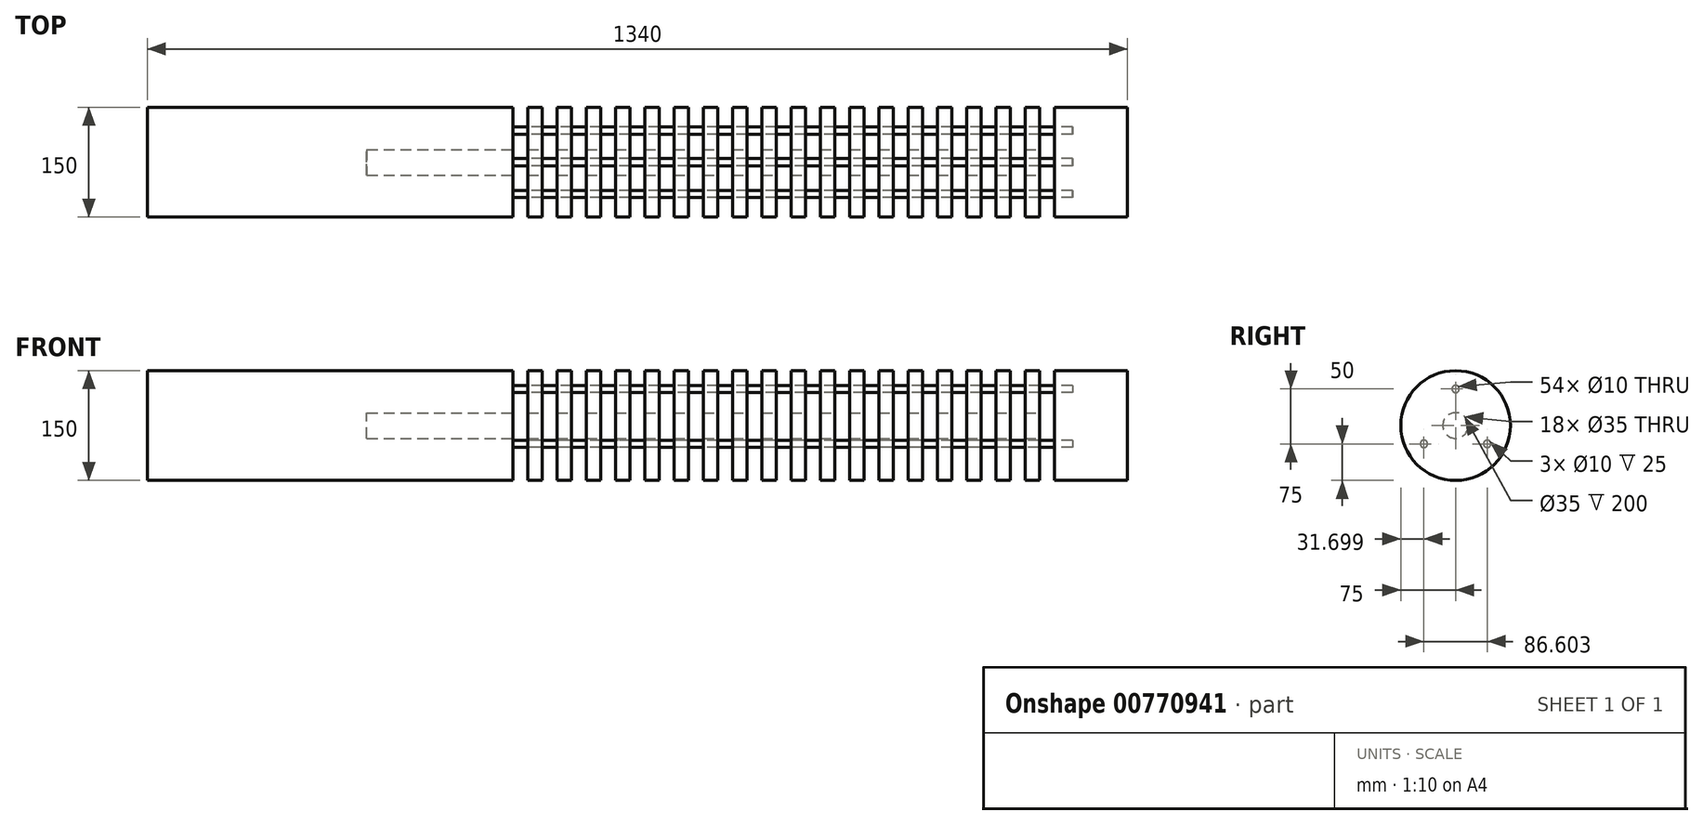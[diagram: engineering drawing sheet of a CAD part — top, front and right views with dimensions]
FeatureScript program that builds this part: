
annotation { "Feature Type Name" : "Feature", "Feature Type Description" : "" }
export const myFeature = defineFeature(function(context is Context, id is Id, definition is map)
    precondition{}
    {
        {
            var Q0;
            Q0=qCreatedBy(makeId("Top.planeOp"),FACE);
            var sketch = newSketch(context, id + "F0", { "sketchPlane" : qUnion([Q0])});
            skLineSegment(sketch, "E0", {"start": v(-500, 0) * mm, "end": v(-500, -75) * mm});
            skLineSegment(sketch, "E1", {"start": v(-500, -75) * mm, "end": v(0, -75) * mm});
            skLineSegment(sketch, "E2", {"start": v(0, -75) * mm, "end": v(0, -17.5) * mm});
            skLineSegment(sketch, "E3", {"start": v(0, -17.5) * mm, "end": v(-200, -17.5) * mm});
            skLineSegment(sketch, "E4", {"start": v(-200, -17.5) * mm, "end": v(-200, 0) * mm});
            skLineSegment(sketch, "E5", {"start": v(-200, 0) * mm, "end": v(-500, 0) * mm});
            skSolve(sketch);
        }
        {
            var Q0;
            Q0=qCreatedBy(makeId("Top.planeOp"),FACE);
            var sketch = newSketch(context, id + "F1", { "sketchPlane" : qUnion([Q0])});
            skLineSegment(sketch, "E6.bottom", {"start": v(20, -17.5) * mm, "end": v(40, -17.5) * mm});
            skLineSegment(sketch, "E6.top", {"start": v(20, -75) * mm, "end": v(40, -75) * mm});
            skLineSegment(sketch, "E6.left", {"start": v(20, -17.5) * mm, "end": v(20, -75) * mm});
            skLineSegment(sketch, "E6.right", {"start": v(40, -17.5) * mm, "end": v(40, -75) * mm});
            skLineSegment(sketch, "E7.1.0.0", {"start": v(60, -75) * mm, "end": v(80, -75) * mm});
            skLineSegment(sketch, "E7.1.0.1", {"start": v(80, -17.5) * mm, "end": v(80, -75) * mm});
            skLineSegment(sketch, "E7.1.0.2", {"start": v(60, -17.5) * mm, "end": v(60, -75) * mm});
            skLineSegment(sketch, "E7.1.0.3", {"start": v(60, -17.5) * mm, "end": v(80, -17.5) * mm});
            skLineSegment(sketch, "E7.2.0.0", {"start": v(100, -75) * mm, "end": v(120, -75) * mm});
            skLineSegment(sketch, "E7.2.0.1", {"start": v(120, -17.5) * mm, "end": v(120, -75) * mm});
            skLineSegment(sketch, "E7.2.0.2", {"start": v(100, -17.5) * mm, "end": v(100, -75) * mm});
            skLineSegment(sketch, "E7.2.0.3", {"start": v(100, -17.5) * mm, "end": v(120, -17.5) * mm});
            skLineSegment(sketch, "E7.3.0.0", {"start": v(140, -75) * mm, "end": v(160, -75) * mm});
            skLineSegment(sketch, "E7.3.0.1", {"start": v(160, -17.5) * mm, "end": v(160, -75) * mm});
            skLineSegment(sketch, "E7.3.0.2", {"start": v(140, -17.5) * mm, "end": v(140, -75) * mm});
            skLineSegment(sketch, "E7.3.0.3", {"start": v(140, -17.5) * mm, "end": v(160, -17.5) * mm});
            skLineSegment(sketch, "E7.4.0.0", {"start": v(180, -75) * mm, "end": v(200, -75) * mm});
            skLineSegment(sketch, "E7.4.0.1", {"start": v(200, -17.5) * mm, "end": v(200, -75) * mm});
            skLineSegment(sketch, "E7.4.0.2", {"start": v(180, -17.5) * mm, "end": v(180, -75) * mm});
            skLineSegment(sketch, "E7.4.0.3", {"start": v(180, -17.5) * mm, "end": v(200, -17.5) * mm});
            skLineSegment(sketch, "E7.5.0.0", {"start": v(220, -75) * mm, "end": v(240, -75) * mm});
            skLineSegment(sketch, "E7.5.0.1", {"start": v(240, -17.5) * mm, "end": v(240, -75) * mm});
            skLineSegment(sketch, "E7.5.0.2", {"start": v(220, -17.5) * mm, "end": v(220, -75) * mm});
            skLineSegment(sketch, "E7.5.0.3", {"start": v(220, -17.5) * mm, "end": v(240, -17.5) * mm});
            skLineSegment(sketch, "E7.6.0.0", {"start": v(260, -75) * mm, "end": v(280, -75) * mm});
            skLineSegment(sketch, "E7.6.0.1", {"start": v(280, -17.5) * mm, "end": v(280, -75) * mm});
            skLineSegment(sketch, "E7.6.0.2", {"start": v(260, -17.5) * mm, "end": v(260, -75) * mm});
            skLineSegment(sketch, "E7.6.0.3", {"start": v(260, -17.5) * mm, "end": v(280, -17.5) * mm});
            skLineSegment(sketch, "E7.7.0.0", {"start": v(300, -75) * mm, "end": v(320, -75) * mm});
            skLineSegment(sketch, "E7.7.0.1", {"start": v(320, -17.5) * mm, "end": v(320, -75) * mm});
            skLineSegment(sketch, "E7.7.0.2", {"start": v(300, -17.5) * mm, "end": v(300, -75) * mm});
            skLineSegment(sketch, "E7.7.0.3", {"start": v(300, -17.5) * mm, "end": v(320, -17.5) * mm});
            skLineSegment(sketch, "E7.8.0.0", {"start": v(340, -75) * mm, "end": v(360, -75) * mm});
            skLineSegment(sketch, "E7.8.0.1", {"start": v(360, -17.5) * mm, "end": v(360, -75) * mm});
            skLineSegment(sketch, "E7.8.0.2", {"start": v(340, -17.5) * mm, "end": v(340, -75) * mm});
            skLineSegment(sketch, "E7.8.0.3", {"start": v(340, -17.5) * mm, "end": v(360, -17.5) * mm});
            skLineSegment(sketch, "E7.9.0.0", {"start": v(380, -75) * mm, "end": v(400, -75) * mm});
            skLineSegment(sketch, "E7.9.0.1", {"start": v(400, -17.5) * mm, "end": v(400, -75) * mm});
            skLineSegment(sketch, "E7.9.0.2", {"start": v(380, -17.5) * mm, "end": v(380, -75) * mm});
            skLineSegment(sketch, "E7.9.0.3", {"start": v(380, -17.5) * mm, "end": v(400, -17.5) * mm});
            skLineSegment(sketch, "E7.10.0.0", {"start": v(420, -75) * mm, "end": v(440, -75) * mm});
            skLineSegment(sketch, "E7.10.0.1", {"start": v(440, -17.5) * mm, "end": v(440, -75) * mm});
            skLineSegment(sketch, "E7.10.0.2", {"start": v(420, -17.5) * mm, "end": v(420, -75) * mm});
            skLineSegment(sketch, "E7.10.0.3", {"start": v(420, -17.5) * mm, "end": v(440, -17.5) * mm});
            skLineSegment(sketch, "E7.11.0.0", {"start": v(460, -75) * mm, "end": v(480, -75) * mm});
            skLineSegment(sketch, "E7.11.0.1", {"start": v(480, -17.5) * mm, "end": v(480, -75) * mm});
            skLineSegment(sketch, "E7.11.0.2", {"start": v(460, -17.5) * mm, "end": v(460, -75) * mm});
            skLineSegment(sketch, "E7.11.0.3", {"start": v(460, -17.5) * mm, "end": v(480, -17.5) * mm});
            skLineSegment(sketch, "E7.12.0.0", {"start": v(500, -75) * mm, "end": v(520, -75) * mm});
            skLineSegment(sketch, "E7.12.0.1", {"start": v(520, -17.5) * mm, "end": v(520, -75) * mm});
            skLineSegment(sketch, "E7.12.0.2", {"start": v(500, -17.5) * mm, "end": v(500, -75) * mm});
            skLineSegment(sketch, "E7.12.0.3", {"start": v(500, -17.5) * mm, "end": v(520, -17.5) * mm});
            skLineSegment(sketch, "E7.13.0.0", {"start": v(540, -75) * mm, "end": v(560, -75) * mm});
            skLineSegment(sketch, "E7.13.0.1", {"start": v(560, -17.5) * mm, "end": v(560, -75) * mm});
            skLineSegment(sketch, "E7.13.0.2", {"start": v(540, -17.5) * mm, "end": v(540, -75) * mm});
            skLineSegment(sketch, "E7.13.0.3", {"start": v(540, -17.5) * mm, "end": v(560, -17.5) * mm});
            skLineSegment(sketch, "E7.14.0.0", {"start": v(580, -75) * mm, "end": v(600, -75) * mm});
            skLineSegment(sketch, "E7.14.0.1", {"start": v(600, -17.5) * mm, "end": v(600, -75) * mm});
            skLineSegment(sketch, "E7.14.0.2", {"start": v(580, -17.5) * mm, "end": v(580, -75) * mm});
            skLineSegment(sketch, "E7.14.0.3", {"start": v(580, -17.5) * mm, "end": v(600, -17.5) * mm});
            skLineSegment(sketch, "E7.15.0.0", {"start": v(620, -75) * mm, "end": v(640, -75) * mm});
            skLineSegment(sketch, "E7.15.0.1", {"start": v(640, -17.5) * mm, "end": v(640, -75) * mm});
            skLineSegment(sketch, "E7.15.0.2", {"start": v(620, -17.5) * mm, "end": v(620, -75) * mm});
            skLineSegment(sketch, "E7.15.0.3", {"start": v(620, -17.5) * mm, "end": v(640, -17.5) * mm});
            skLineSegment(sketch, "E7.16.0.0", {"start": v(660, -75) * mm, "end": v(680, -75) * mm});
            skLineSegment(sketch, "E7.16.0.1", {"start": v(680, -17.5) * mm, "end": v(680, -75) * mm});
            skLineSegment(sketch, "E7.16.0.2", {"start": v(660, -17.5) * mm, "end": v(660, -75) * mm});
            skLineSegment(sketch, "E7.16.0.3", {"start": v(660, -17.5) * mm, "end": v(680, -17.5) * mm});
            skLineSegment(sketch, "E7.17.0.0", {"start": v(700, -75) * mm, "end": v(720, -75) * mm});
            skLineSegment(sketch, "E7.17.0.1", {"start": v(720, -17.5) * mm, "end": v(720, -75) * mm});
            skLineSegment(sketch, "E7.17.0.2", {"start": v(700, -17.5) * mm, "end": v(700, -75) * mm});
            skLineSegment(sketch, "E7.17.0.3", {"start": v(700, -17.5) * mm, "end": v(720, -17.5) * mm});
            skLineSegment(sketch, "E7.direction1", {"start": v(20, -75) * mm, "end": v(60, -75) * mm, "construction": true});
            skSolve(sketch);
        }
        {
            var Q0;
            Q0=qCreatedBy(makeId("Top.planeOp"),FACE);
            var sketch = newSketch(context, id + "F2", { "sketchPlane" : qUnion([Q0])});
            skLineSegment(sketch, "E8.bottom", {"start": v(740, -75) * mm, "end": v(840, -75) * mm});
            skLineSegment(sketch, "E8.top", {"start": v(740, 0) * mm, "end": v(840, 0) * mm});
            skLineSegment(sketch, "E8.left", {"start": v(740, -75) * mm, "end": v(740, 0) * mm});
            skLineSegment(sketch, "E8.right", {"start": v(840, -75) * mm, "end": v(840, 0) * mm});
            skSolve(sketch);
        }
        {
            var Q0;
            Q0=makeQuery(id+"F0.imprint","IMPRINT",FACE,{"disambiguationData":[TD([[makeQuery(id+"F0.imprint","IMPRINT",EDGE,{"derivedFrom":sQuery(id+"F0.wireOp",EDGE,"E0")}),1.0]])]});
            var Q1;
            Q1=makeQuery(id+"F1.imprint","IMPRINT",FACE,{"disambiguationData":[TD([[makeQuery(id+"F1.imprint","IMPRINT",EDGE,{"derivedFrom":sQuery(id+"F1.wireOp",EDGE,"E7.4.0.0")}),1.0]])]});
            var Q2;
            Q2=makeQuery(id+"F1.imprint","IMPRINT",FACE,{"disambiguationData":[TD([[makeQuery(id+"F1.imprint","IMPRINT",EDGE,{"derivedFrom":sQuery(id+"F1.wireOp",EDGE,"E7.9.0.0")}),1.0]])]});
            var Q3;
            Q3=makeQuery(id+"F1.imprint","IMPRINT",FACE,{"disambiguationData":[TD([[makeQuery(id+"F1.imprint","IMPRINT",EDGE,{"derivedFrom":sQuery(id+"F1.wireOp",EDGE,"E7.3.0.0")}),1.0]])]});
            var Q4;
            Q4=makeQuery(id+"F1.imprint","IMPRINT",FACE,{"disambiguationData":[TD([[makeQuery(id+"F1.imprint","IMPRINT",EDGE,{"derivedFrom":sQuery(id+"F1.wireOp",EDGE,"E7.2.0.0")}),1.0]])]});
            var Q5;
            Q5=makeQuery(id+"F1.imprint","IMPRINT",FACE,{"disambiguationData":[TD([[makeQuery(id+"F1.imprint","IMPRINT",EDGE,{"derivedFrom":sQuery(id+"F1.wireOp",EDGE,"E7.10.0.0")}),1.0]])]});
            var Q6;
            Q6=makeQuery(id+"F1.imprint","IMPRINT",FACE,{"disambiguationData":[TD([[makeQuery(id+"F1.imprint","IMPRINT",EDGE,{"derivedFrom":sQuery(id+"F1.wireOp",EDGE,"E7.1.0.0")}),1.0]])]});
            var Q7;
            Q7=makeQuery(id+"F1.imprint","IMPRINT",FACE,{"disambiguationData":[TD([[makeQuery(id+"F1.imprint","IMPRINT",EDGE,{"derivedFrom":sQuery(id+"F1.wireOp",EDGE,"E7.8.0.0")}),1.0]])]});
            var Q8;
            Q8=makeQuery(id+"F1.imprint","IMPRINT",FACE,{"disambiguationData":[TD([[makeQuery(id+"F1.imprint","IMPRINT",EDGE,{"derivedFrom":sQuery(id+"F1.wireOp",EDGE,"E7.17.0.0")}),1.0]])]});
            var Q9;
            Q9=makeQuery(id+"F1.imprint","IMPRINT",FACE,{"disambiguationData":[TD([[makeQuery(id+"F1.imprint","IMPRINT",EDGE,{"derivedFrom":sQuery(id+"F1.wireOp",EDGE,"E7.16.0.0")}),1.0]])]});
            var Q10;
            Q10=makeQuery(id+"F1.imprint","IMPRINT",FACE,{"disambiguationData":[TD([[makeQuery(id+"F1.imprint","IMPRINT",EDGE,{"derivedFrom":sQuery(id+"F1.wireOp",EDGE,"E7.12.0.0")}),1.0]])]});
            var Q11;
            Q11=makeQuery(id+"F1.imprint","IMPRINT",FACE,{"disambiguationData":[TD([[makeQuery(id+"F1.imprint","IMPRINT",EDGE,{"derivedFrom":sQuery(id+"F1.wireOp",EDGE,"E7.5.0.0")}),1.0]])]});
            var Q12;
            Q12=makeQuery(id+"F1.imprint","IMPRINT",FACE,{"disambiguationData":[TD([[makeQuery(id+"F1.imprint","IMPRINT",EDGE,{"derivedFrom":sQuery(id+"F1.wireOp",EDGE,"E7.6.0.0")}),1.0]])]});
            var Q13;
            Q13=makeQuery(id+"F1.imprint","IMPRINT",FACE,{"disambiguationData":[TD([[makeQuery(id+"F1.imprint","IMPRINT",EDGE,{"derivedFrom":sQuery(id+"F1.wireOp",EDGE,"E7.11.0.0")}),1.0]])]});
            var Q14;
            Q14=makeQuery(id+"F1.imprint","IMPRINT",FACE,{"disambiguationData":[TD([[makeQuery(id+"F1.imprint","IMPRINT",EDGE,{"derivedFrom":sQuery(id+"F1.wireOp",EDGE,"E7.7.0.0")}),1.0]])]});
            var Q15;
            Q15=makeQuery(id+"F1.imprint","IMPRINT",FACE,{"disambiguationData":[TD([[makeQuery(id+"F1.imprint","IMPRINT",EDGE,{"derivedFrom":sQuery(id+"F1.wireOp",EDGE,"E6.bottom")}),-1.0]])]});
            var Q16;
            Q16=makeQuery(id+"F1.imprint","IMPRINT",FACE,{"disambiguationData":[TD([[makeQuery(id+"F1.imprint","IMPRINT",EDGE,{"derivedFrom":sQuery(id+"F1.wireOp",EDGE,"E7.14.0.0")}),1.0]])]});
            var Q17;
            Q17=makeQuery(id+"F1.imprint","IMPRINT",FACE,{"disambiguationData":[TD([[makeQuery(id+"F1.imprint","IMPRINT",EDGE,{"derivedFrom":sQuery(id+"F1.wireOp",EDGE,"E7.13.0.0")}),1.0]])]});
            var Q18;
            Q18=makeQuery(id+"F2.imprint","IMPRINT",FACE,{"disambiguationData":[TD([[makeQuery(id+"F2.imprint","IMPRINT",EDGE,{"derivedFrom":sQuery(id+"F2.wireOp",EDGE,"E8.bottom")}),1.0]])]});
            var Q19;
            Q19=makeQuery(id+"F1.imprint","IMPRINT",FACE,{"disambiguationData":[TD([[makeQuery(id+"F1.imprint","IMPRINT",EDGE,{"derivedFrom":sQuery(id+"F1.wireOp",EDGE,"E7.15.0.0")}),1.0]])]});
            var Q20;
            Q20=sQuery(id+"F0.wireOp",EDGE,"E5");
            revolve(context, id + "F3", {"surfaceOperationType" : NewSurfaceOperationType.NEW, "entities" : qUnion([Q0, Q1, Q2, Q3, Q4, Q5, Q6, Q7, Q8, Q9, Q10, Q11, Q12, Q13, Q14, Q15, Q16, Q17, Q18, Q19]), "axis" : qUnion([Q20]), "revolveType" : RevolveType.FULL});
        }
        {
            var Q0;
            Q0=qCreatedBy(makeId("Right.planeOp"),FACE);
            var sketch = newSketch(context, id + "F4", { "sketchPlane" : qUnion([Q0])});
            skCircle(sketch, "E9", {"center": v(0, 50) * mm, "radius": 5 * mm});
            skCircle(sketch, "E10.1.0", {"center": v(-43.3, -25) * mm, "radius": 5 * mm});
            skCircle(sketch, "E10.2.0", {"center": v(43.3, -25) * mm, "radius": 5 * mm});
            skPoint(sketch, "E10.center", {"position": v(0, 0) * mm});
            skSolve(sketch);
        }
        {
            var Q0;
            Q0=qSketchRegion(id+"F4",true);
            var Q1;
            Q1=makeQuery(id+"F3.opRevolve","SWEPT_FACE",FACE,{"disambiguationData":[OSD([sQuery(id+"F2.wireOp",EDGE,"E8.left")])]});
            extrude(context, id + "F5", {"entities" : qUnion([Q0]), "operationType" : NewBodyOperationType.REMOVE, "endBound" : BoundingType.UP_TO_SURFACE, "depth" : 25 * mm, "endBoundEntityFace" : qUnion([Q1]), "hasOffset" : true, "offsetDistance" : 25 * mm, "offsetOppositeDirection" : true});
        }
        {
            var Q0;
            Q0 = qSketchRegion(id + "F4", true);
            var Q1;
            Q1=makeQuery(id+"F3.opRevolve","SWEPT_FACE",FACE,{"disambiguationData":[OSD([sQuery(id+"F2.wireOp",EDGE,"E8.left")])]});
            extrude(context, id + "F6", {"entities" : qUnion([Q0]), "endBound" : BoundingType.UP_TO_SURFACE, "depth" : 25 * mm, "endBoundEntityFace" : qUnion([Q1]), "hasOffset" : true, "offsetDistance" : 25 * mm, "offsetOppositeDirection" : true});
        }
        {
            var Q0;
            Q0 = qSketchRegion(id + "F2", true);
            var Q1;
            Q1=sQuery(id+"F2.wireOp",EDGE,"E8.top");
            revolve(context, id + "F7", {"surfaceOperationType" : NewSurfaceOperationType.NEW, "entities" : qUnion([Q0]), "axis" : qUnion([Q1]), "revolveType" : RevolveType.FULL});
        }
    });
